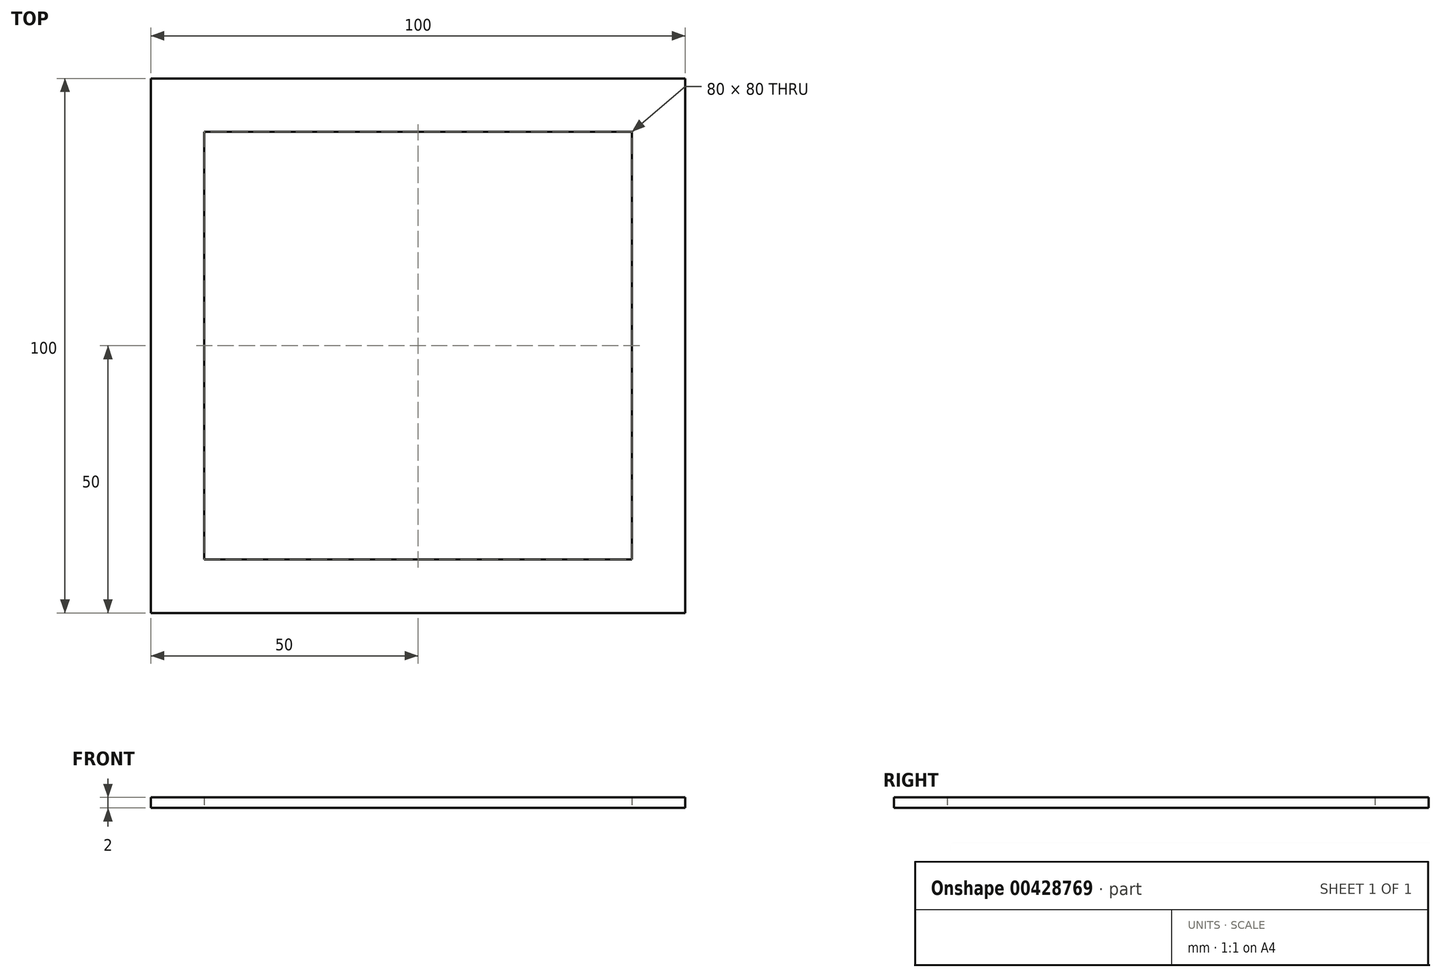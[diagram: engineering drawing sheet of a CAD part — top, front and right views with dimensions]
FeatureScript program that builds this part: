
annotation { "Feature Type Name" : "Feature", "Feature Type Description" : "" }
export const myFeature = defineFeature(function(context is Context, id is Id, definition is map)
    precondition{}
    {
        {
            var Q0;
            Q0=qCreatedBy(makeId("Top.planeOp"),FACE);
            var sketch = newSketch(context, id + "F0", { "sketchPlane" : qUnion([Q0])});
            skPoint(sketch, "E0", {"position": v(-50, 50) * mm});
            skLineSegment(sketch, "E1.bottom", {"start": v(-50, 50) * mm, "end": v(50, 50) * mm});
            skLineSegment(sketch, "E1.top", {"start": v(-50, -50) * mm, "end": v(50, -50) * mm});
            skLineSegment(sketch, "E1.left", {"start": v(-50, 50) * mm, "end": v(-50, -50) * mm});
            skLineSegment(sketch, "E1.right", {"start": v(50, 50) * mm, "end": v(50, -50) * mm});
            skLineSegment(sketch, "E2.bottom", {"start": v(-40, 40) * mm, "end": v(40, 40) * mm});
            skLineSegment(sketch, "E2.top", {"start": v(-40, -40) * mm, "end": v(40, -40) * mm});
            skLineSegment(sketch, "E2.left", {"start": v(-40, 40) * mm, "end": v(-40, -40) * mm});
            skLineSegment(sketch, "E2.right", {"start": v(40, 40) * mm, "end": v(40, -40) * mm});
            skSolve(sketch);
        }
        {
            var Q0;
            Q0 = qSketchRegion(id + "F0", true);
            extrude(context, id + "F1", {"entities" : qUnion([Q0]), "depth" : 2 * mm});
        }
    });
